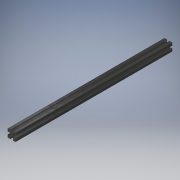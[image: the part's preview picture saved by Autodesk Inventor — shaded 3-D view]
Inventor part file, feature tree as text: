
AUTODESK INVENTOR PART (.ipt)
format: ipt  version: 2019 (Build 230136000, 136)  size: 235,520 bytes
history: native  units: in
note: dims shown in document units (in); Inventor stores cm internally (conversion verified against a paired STEP export)
features: fillet x2, thread x2, extrude x1, sketch x1
ambient origin geometry x8: Origin, YZ Plane, XZ Plane, XY Plane, X Axis, Y Axis, Z Axis, Center Point
bodies: Solid1 (feature_tree)
feature tree (6):
  extrude  "Extrusion1"  Depth=0.3937in
  fillet  "Fillet1"  Radius=0.1378in
  fillet  "Fillet2"  Radius=0.0394in
  thread  "Thread1"  [1 undecoded]
  thread  "Thread2"  [1 undecoded]
  sketch  "Sketch1"  dims[d0=0.0984in d1=0.3937in d2=0.3937in d3=0.1378in d4=0.0394in d5=90.0deg d6=0.1378in d10=0.0787in d11=0.2749in d13=0.3436in d14=0.0394in d15=1.5748in d17=360.0deg d19=0.1225in d21=7.874in d22=0.0in d23=0.0071in d24=0.0118in d25=0.315in d26=0.0in d27=0.315in d28=0.0in]
note: 2 required parameter values undecoded (feature->parameter linkage not recoverable at this tier; creation-order binding heuristic only, values carry confidence <= 0.55)
